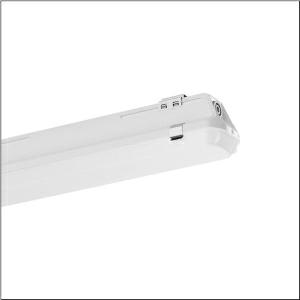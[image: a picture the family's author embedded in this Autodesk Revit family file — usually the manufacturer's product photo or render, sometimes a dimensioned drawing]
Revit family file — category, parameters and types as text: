
# Revit family: monsun_r__21_emergency_51fb107p437b3g_111f
name_source: partatom
category: Lighting Fixtures
units: mm (PartAtom-declared; Revit-internal decimal feet)

## family parameters
Cut with Voids When Loaded = No
Host = Face
Light Source = No
Part Type = Normal
Room Calculation Point = No
Round Connector Dimension = Use Diameter
Shared = No

## types (1)
- Monsun® 21 emergency (1 x LED, 3860 lm, 26.9 W, 4000K)
    Apparent Load = 27 VA
    CIE Flux Codes = 47 77 93 94 100
    Color Rendering = 80
    Color Temperature = 4000K
    Default Elevation = 1800 mm
    Description = Monsun® 21 emergency, damp-proof luminaire, chain hanger, primary optical cover: enclosure, of PMMA, light emission: direct distribution, primary light characteristic: symmetric, installation type: vertical mounting, horizontal mounting, surface-mounted, suspended mounting, LED, rated luminous flux: 3.860lm, luminous efficacy: 144lm/W, light colour: 840, colour temperature: 4000K, control gear: ECG, with terminal, 4-pole, max. 2.5mm², mains connection: 220..240V, AC, 50/60Hz, rated input power: 27W, control gear: single battery element, battery: NiCd, 4,5Ah, mains connection: 230V, housing, of glass-fibre reinforced polyester, uncoated, bright grey, incl. chain hanger, length: 1.590mm, width: 90mm, height: 88mm, clip for enclosure, of stainless steel (V2A), ceiling mounting element, of stainless steel (V2A), chain hanger, of stainless steel (V2A), protection rating (complete): IP66, insulation class (complete): insulation class I (protective earthing), certification: CE, UKCA, protection symbol: D, impact resistance: IK04, permissible operating ambient temperature: +5..+25°C, standard: EN 60598-2-1, EN 50419, EN 60598-2-22, corresponds to IFS (International Featured Standards) requirements for safety and quality in the food industry, for indoor or canopied outdoor use, no direct snow, no direct sun, no direct rain, contact your sales advisor before using the luminaires in applications with unclear chemical exposure, large temperature fluctuations or condensation-forming humidity, LABS conformity tested according to VDMA 24364:2018-05, packaging unit: 1 piece
    Height = 89 mm
    Lamp = 1 x LED
    Lamp Light Flux = 3860 lm
    Lamp Power = 26.9 W
    Lamp count = 1
    Length = 1590 mm
    Luminous efficacy = 143 lm/W
    Manufacturer = Siteco
    ModVariant = No
    Model = 51FB107P437B3G
    Mounting Place = Ceiling
    Mounting Type = Surface mounted
    Number of Poles = 1
    OnlyDefault = Yes
    Power Factor = 1
    Product Name = Monsun® 21 emergency
    Product group = damp-proof luminaire
    ProductGroupID = 300
    Protection Class = Protection class I
    Protection Degree = IP 66
    RLX_Detail_Level = 1
    RLX_Emergency_Light_Flux = 0 lm
    RLX_Emergency_Type = 0
    RLX_Emergency_Type_DB = No
    RlxData = <blob elided: 89017 chars, md5=72aea74b>
    Socket = socket
    Standby Power = 0 W
    System Light Flux = 3860 lm
    System Power = 27 W
    Type Comments = Product without accessories
    Type Image = l_1006717.jpg
    URL = http://relux.com
    VarID = ---
    Voltage = 0 V
    Weight = 0.00 kg
    Width = 90 mm

## geometry (parser evidence)
native form markers: Blend x4, Sweep x12
no freeform markers — native parametric forms only
